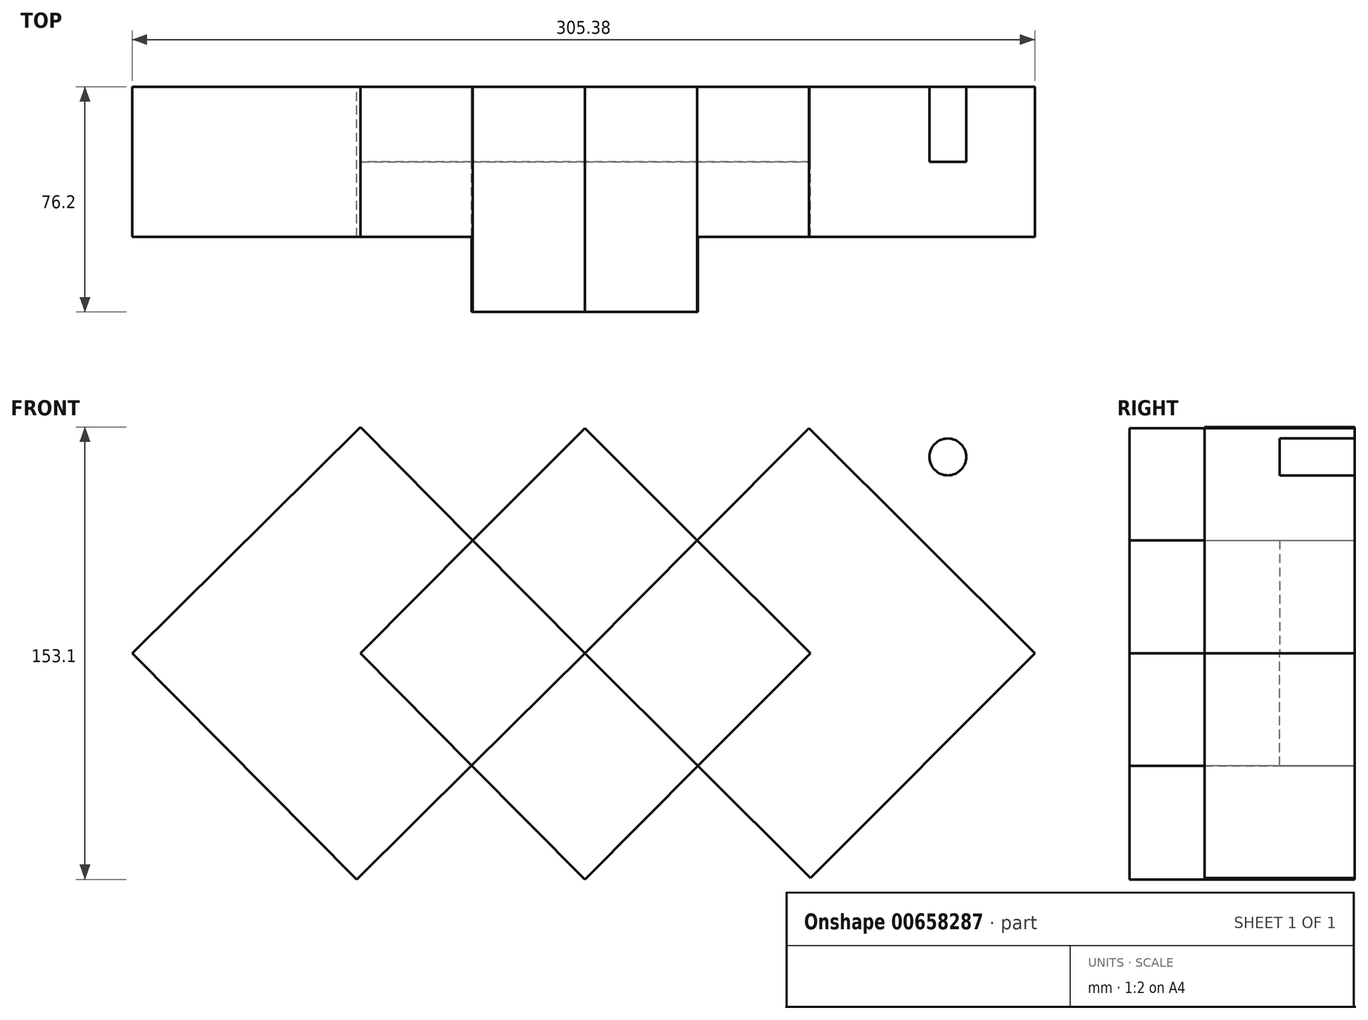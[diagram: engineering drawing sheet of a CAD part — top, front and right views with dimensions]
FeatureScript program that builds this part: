
annotation { "Feature Type Name" : "Feature", "Feature Type Description" : "" }
export const myFeature = defineFeature(function(context is Context, id is Id, definition is map)
    precondition{}
    {
        {
            var Q0;
            Q0=qCreatedBy(makeId("Front.planeOp"),FACE);
            var sketch = newSketch(context, id + "F0", { "sketchPlane" : qUnion([Q0])});
            skLineSegment(sketch, "E0", {"start": v(-75.93, 0) * mm, "end": v(0, 76.14) * mm});
            skLineSegment(sketch, "E1", {"start": v(0, 76.14) * mm, "end": v(76.34, 0) * mm});
            skLineSegment(sketch, "E2", {"start": v(76.34, 0) * mm, "end": v(0, -76.55) * mm});
            skLineSegment(sketch, "E3", {"start": v(0, -76.55) * mm, "end": v(-75.93, 0) * mm});
            skLineSegment(sketch, "E4", {"start": v(0, 0) * mm, "end": v(75.93, 76.14) * mm});
            skLineSegment(sketch, "E5", {"start": v(75.93, 76.14) * mm, "end": v(152.27, 0) * mm});
            skLineSegment(sketch, "E6", {"start": v(152.27, 0) * mm, "end": v(76.34, -76.14) * mm});
            skLineSegment(sketch, "E7", {"start": v(76.34, -76.14) * mm, "end": v(0, 0) * mm});
            skLineSegment(sketch, "E8", {"start": v(0, 0) * mm, "end": v(-77.18, -76.55) * mm});
            skLineSegment(sketch, "E9", {"start": v(-77.18, -76.55) * mm, "end": v(-153.11, 0) * mm});
            skLineSegment(sketch, "E10", {"start": v(-153.11, 0) * mm, "end": v(-75.93, 76.55) * mm});
            skLineSegment(sketch, "E11", {"start": v(-75.93, 76.55) * mm, "end": v(0, 0) * mm});
            skSolve(sketch);
        }
        {
            var Q0;
            {var subQ0=sQuery(id+"F0.wireOp",EDGE,"E3");var subQ1=sQuery(id+"F0.wireOp",EDGE,"E0");var subQ2=makeQuery(id+"F0.imprint","INTERSECT",VERTEX,{"derivedFrom":[subQ1,subQ0]});Q0=makeQuery(id+"F0.imprint","IMPRINT",FACE,{"disambiguationData":[TD([[makeQuery(id+"F0.imprint","IMPRINT",EDGE,{"disambiguationData":[TD([[subQ2,-1.0]])],"derivedFrom":subQ1}),-1.0]])]});}
            var Q1;
            {var subQ0=sQuery(id+"F0.wireOp",EDGE,"E2");var subQ1=sQuery(id+"F0.wireOp",EDGE,"E1");var subQ2=makeQuery(id+"F0.imprint","INTERSECT",VERTEX,{"derivedFrom":[subQ1,subQ0]});Q1=makeQuery(id+"F0.imprint","IMPRINT",FACE,{"disambiguationData":[TD([[makeQuery(id+"F0.imprint","IMPRINT",EDGE,{"disambiguationData":[TD([[subQ2,1.0]])],"derivedFrom":subQ1}),-1.0]])]});}
            extrude(context, id + "F1", {"entities" : qUnion([Q0, Q1]), "depth" : 25.4 * mm, "offsetDistance" : 25.4 * mm});
        }
        {
            var Q0;
            {var subQ0=sQuery(id+"F0.wireOp",EDGE,"E9");Q0=makeQuery(id+"F0.imprint","IMPRINT",FACE,{"disambiguationData":[TD([[makeQuery(id+"F0.imprint","IMPRINT",EDGE,{"derivedFrom":subQ0}),-1.0]])]});}
            var Q1;
            {var subQ0=sQuery(id+"F0.wireOp",EDGE,"E5");Q1=makeQuery(id+"F0.imprint","IMPRINT",FACE,{"disambiguationData":[TD([[makeQuery(id+"F0.imprint","IMPRINT",EDGE,{"derivedFrom":subQ0}),-1.0]])]});}
            extrude(context, id + "F2", {"entities" : qUnion([Q0, Q1]), "depth" : 50.8 * mm, "offsetDistance" : 25.4 * mm});
        }
        {
            var Q0;
            {var subQ0=sQuery(id+"F0.wireOp",EDGE,"E1");var subQ1=sQuery(id+"F0.wireOp",EDGE,"E0");var subQ2=makeQuery(id+"F0.imprint","INTERSECT",VERTEX,{"derivedFrom":[subQ1,subQ0]});Q0=makeQuery(id+"F0.imprint","IMPRINT",FACE,{"disambiguationData":[TD([[makeQuery(id+"F0.imprint","IMPRINT",EDGE,{"disambiguationData":[TD([[subQ2,1.0]])],"derivedFrom":subQ1}),-1.0]])]});}
            var Q1;
            {var subQ0=sQuery(id+"F0.wireOp",EDGE,"E3");var subQ1=sQuery(id+"F0.wireOp",EDGE,"E2");var subQ2=makeQuery(id+"F0.imprint","INTERSECT",VERTEX,{"derivedFrom":[subQ1,subQ0]});Q1=makeQuery(id+"F0.imprint","IMPRINT",FACE,{"disambiguationData":[TD([[makeQuery(id+"F0.imprint","IMPRINT",EDGE,{"disambiguationData":[TD([[subQ2,1.0]])],"derivedFrom":subQ1}),-1.0]])]});}
            extrude(context, id + "F3", {"entities" : qUnion([Q0, Q1]), "depth" : 76.2 * mm, "offsetDistance" : 25.4 * mm});
        }
        {
            var Q0;
            Q0=qCreatedBy(makeId("Front.planeOp"),FACE);
            var sketch = newSketch(context, id + "F4", { "sketchPlane" : qUnion([Q0])});
            skCircle(sketch, "E12", {"center": v(122.83, 66.47) * mm, "radius": 6.23 * mm});
            skSolve(sketch);
        }
        {
            var Q0;
            Q0 = qSketchRegion(id + "F4", true);
            extrude(context, id + "F5", {"entities" : qUnion([Q0]), "depth" : 25.4 * mm, "offsetDistance" : 25.4 * mm});
        }
    });
